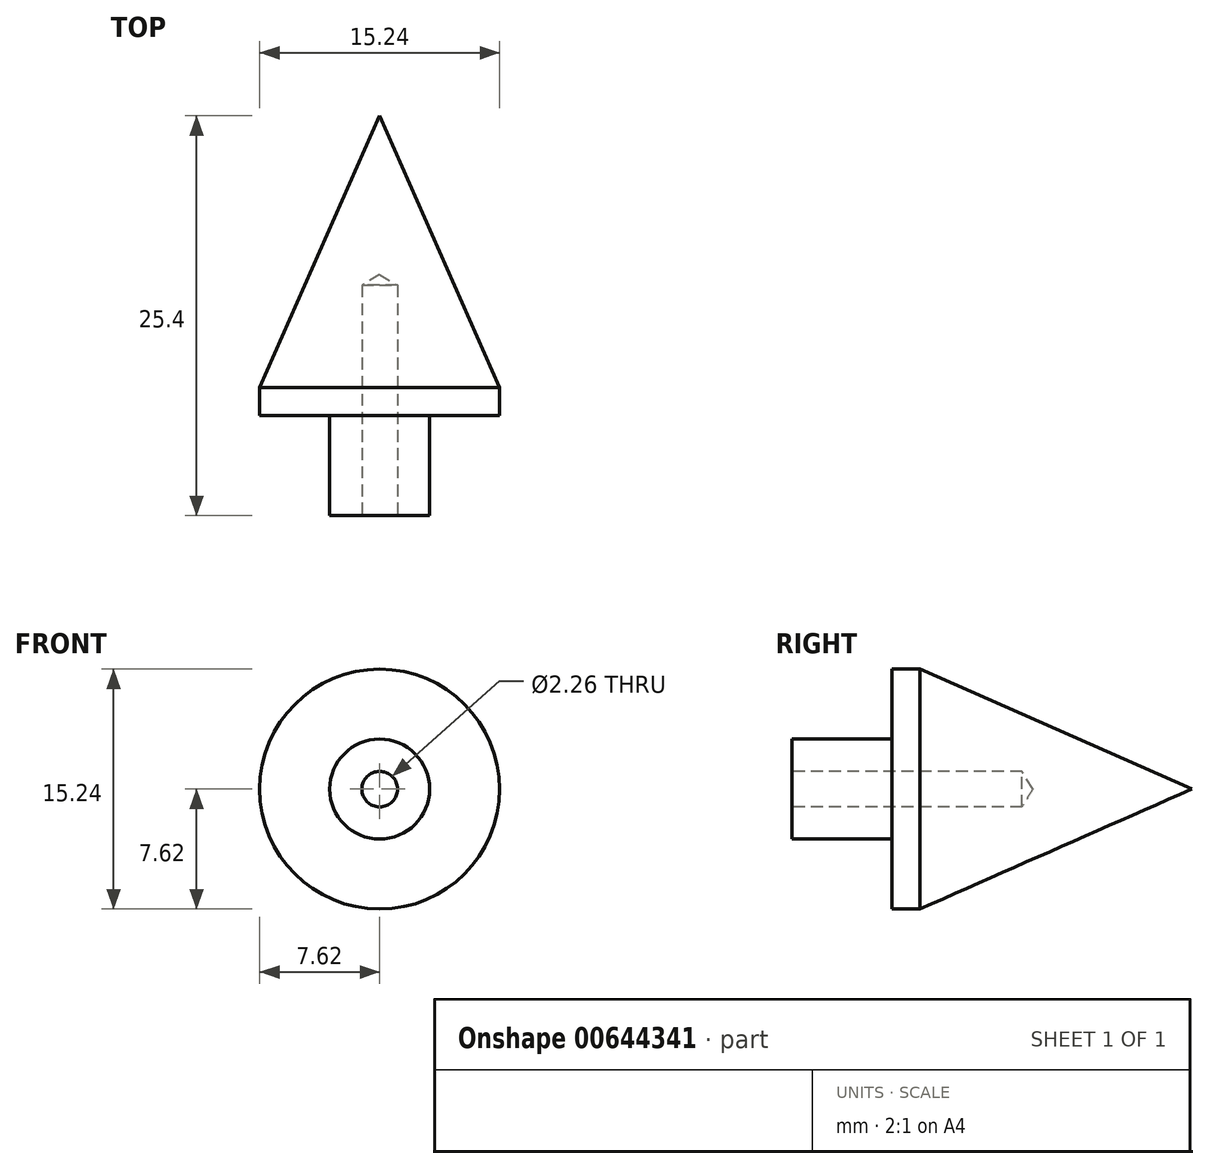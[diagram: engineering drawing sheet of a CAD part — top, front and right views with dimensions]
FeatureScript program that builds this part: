
annotation { "Feature Type Name" : "Feature", "Feature Type Description" : "" }
export const myFeature = defineFeature(function(context is Context, id is Id, definition is map)
    precondition{}
    {
        {
            var Q0;
            Q0=qCreatedBy(makeId("Top.planeOp"),FACE);
            var sketch = newSketch(context, id + "F0", { "sketchPlane" : qUnion([Q0])});
            skLineSegment(sketch, "E0", {"start": v(0, 0) * mm, "end": v(0, 25.4) * mm});
            skLineSegment(sketch, "E1", {"start": v(7.62, 6.35) * mm, "end": v(3.17, 6.35) * mm});
            skLineSegment(sketch, "E2", {"start": v(3.17, 6.35) * mm, "end": v(3.17, 0) * mm});
            skLineSegment(sketch, "E3", {"start": v(3.17, 0) * mm, "end": v(0, 0) * mm});
            skLineSegment(sketch, "E4", {"start": v(7.62, 6.35) * mm, "end": v(7.62, 8.13) * mm});
            skLineSegment(sketch, "E5", {"start": v(7.62, 8.13) * mm, "end": v(0, 25.4) * mm});
            skSolve(sketch);
        }
        {
            var Q0;
            Q0=makeQuery(id+"F0.imprint","IMPRINT",FACE,{"disambiguationData":[TD([[makeQuery(id+"F0.imprint","IMPRINT",EDGE,{"derivedFrom":sQuery(id+"F0.wireOp",EDGE,"E0")}),-1.0]])]});
            var Q1;
            Q1=sQuery(id+"F0.wireOp",EDGE,"E0");
            revolve(context, id + "F1", {"entities" : qUnion([Q0]), "axis" : qUnion([Q1]), "revolveType" : RevolveType.FULL});
        }
        {
            var Q0;
            Q0=qCreatedBy(makeId("Front.planeOp"),FACE);
            var sketch = newSketch(context, id + "F2", { "sketchPlane" : qUnion([Q0])});
            skPoint(sketch, "E6", {"position": v(0, 0) * mm});
            skSolve(sketch);
        }
        {
            var Q0;
            Q0=sQuery(id+"F2.wireOp",VERTEX,"E6");
            var Q1;
            Q1=makeQuery(id+"F1.opRevolve","SWEPT_BODY",BODY,{"disambiguationData":[OSD([sQuery(id+"F0.wireOp",EDGE,"E0"),sQuery(id+"F0.wireOp",EDGE,"DCKnWAF3-nRJL-w0qp-VUsM-nt4ogAzZi8rr"),sQuery(id+"F0.wireOp",EDGE,"E1"),sQuery(id+"F0.wireOp",EDGE,"E2"),sQuery(id+"F0.wireOp",EDGE,"E3")])]});
            hole(context, id + "F3", {"style" : HoleStyle.SIMPLE, "endStyle" : HoleEndStyle.BLIND, "standardTappedOrClearance" : lookupTablePath({ "standard" : "ANSI", "engagement" : "75%", "pitch" : "40 tpi", "size" : "#4", "type" : "Tapped" }), "standardBlindInLast" : lookupTablePath({ "standard" : "ANSI", "engagement" : "75%", "pitch" : "40 tpi", "size" : "#4", "type" : "Tapped" }), "holeDiameter" : 2.26 * mm, "majorDiameter" : 2.84 * mm, "showTappedDepth" : true, "holeDepth" : 14.63 * mm, "isTappedThrough" : true, "tappedDepth" : 12.73 * mm, "tapClearance" : 3, "locations" : qUnion([Q0]), "scope" : qUnion([Q1])});
        }
    });
